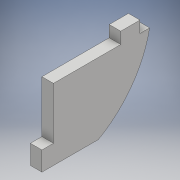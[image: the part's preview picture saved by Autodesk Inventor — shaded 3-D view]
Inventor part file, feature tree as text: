
AUTODESK INVENTOR PART (.ipt)
format: ipt  version: 2017 (Build 210142000, 142)  size: 104,448 bytes
history: native  units: mm
features: extrude x1, sketch x1
ambient origin geometry x8: Origin, YZ Plane, XZ Plane, XY Plane, X Axis, Y Axis, Z Axis, Center Point
bodies: Solide1 (feature_tree)
feature tree (2):
  extrude  "Extrusion1"  Depth=35.0mm
  sketch  "Esquisse1"
